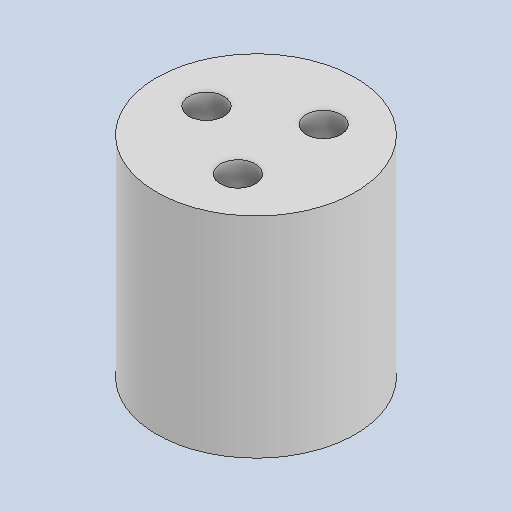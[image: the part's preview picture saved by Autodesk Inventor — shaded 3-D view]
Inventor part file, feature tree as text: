
AUTODESK INVENTOR PART (.ipt)
format: ipt  version: 2025.2 (Build 292293000, 293)  size: 208,384 bytes
history: native  units: mm
features: sketch x3, extrude x2, other x1
ambient origin geometry x8: Origin, YZ Plane, XZ Plane, XY Plane, X Axis, Y Axis, Z Axis, Center Point
bodies: Solid1 (feature_tree)
feature tree (6):
  other  "thigh_joint"
  extrude  "Extrusion1"  Depth=18.0mm TaperAngle=0.0deg
  extrude  "Extrusion2"  Depth=3.0mm
  sketch  "Sketch1"  dims[d0=17.0425mm d1=18.0mm d2=0.0mm]
  sketch  "Sketch2"  dims[d5=30.0mm d7=360.0deg d9=0.0mm d10=0.0mm]
  sketch  "Sketch Circular Pattern1"  dims[d3=8.5mm d4=3.0mm]
